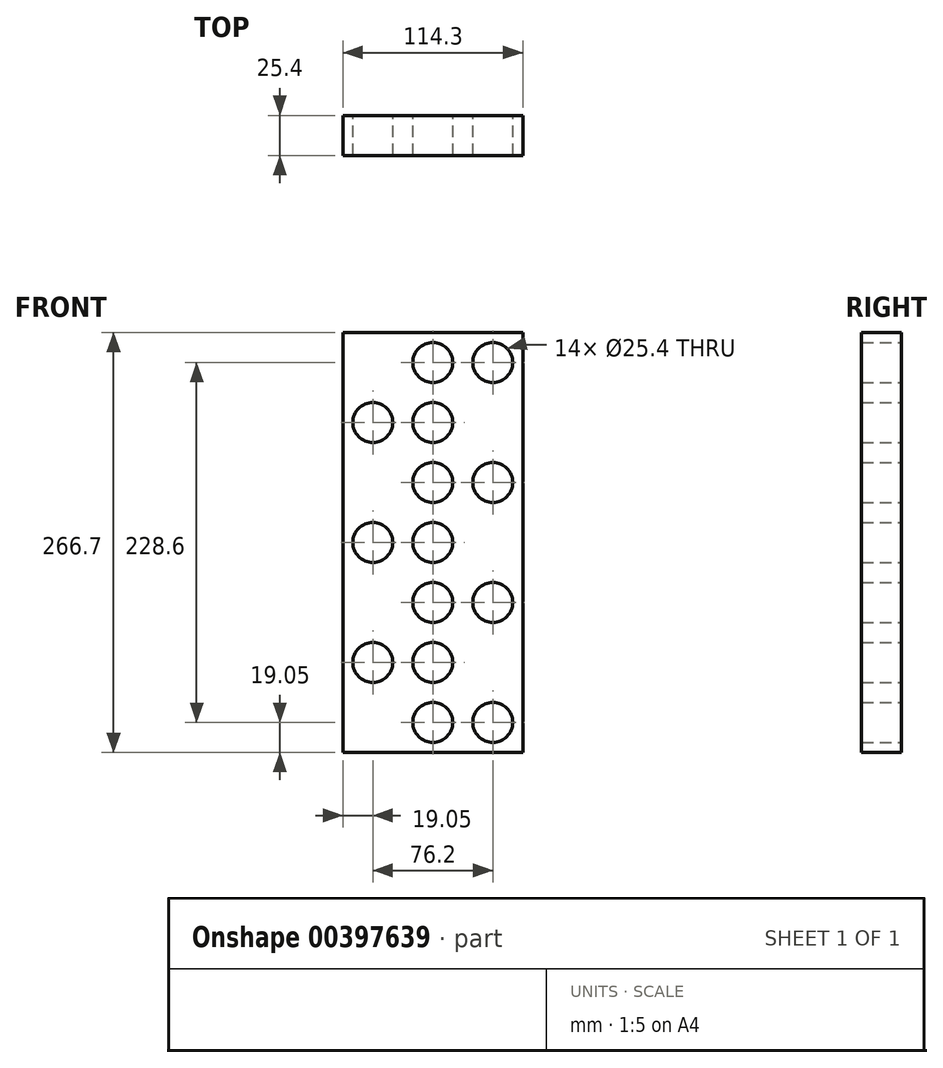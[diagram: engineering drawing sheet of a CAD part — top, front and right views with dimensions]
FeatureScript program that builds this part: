
annotation { "Feature Type Name" : "Feature", "Feature Type Description" : "" }
export const myFeature = defineFeature(function(context is Context, id is Id, definition is map)
    precondition{}
    {
        {
            var Q0;
            Q0=qCreatedBy(makeId("Front.planeOp"),FACE);
            var sketch = newSketch(context, id + "F0", { "sketchPlane" : qUnion([Q0])});
            skLineSegment(sketch, "E0.bottom", {"start": v(0, 0) * mm, "end": v(-114.3, 0) * mm});
            skLineSegment(sketch, "E0.top", {"start": v(0, 266.7) * mm, "end": v(-114.3, 266.7) * mm});
            skLineSegment(sketch, "E0.left", {"start": v(0, 0) * mm, "end": v(0, 266.7) * mm});
            skLineSegment(sketch, "E0.right", {"start": v(-114.3, 0) * mm, "end": v(-114.3, 266.7) * mm});
            skSolve(sketch);
        }
        {
            var Q0;
            Q0=qCreatedBy(makeId("Front.planeOp"),FACE);
            var sketch = newSketch(context, id + "F1", { "sketchPlane" : qUnion([Q0])});
            skLineSegment(sketch, "E1", {"start": v(0, 0) * mm, "end": v(-19.05, 0) * mm});
            skLineSegment(sketch, "E2", {"start": v(0, 0) * mm, "end": v(-57.15, 0) * mm});
            skPoint(sketch, "E2.endSnap0", {"position": v(-9.53, 0) * mm});
            skLineSegment(sketch, "E3", {"start": v(0, 0) * mm, "end": v(-95.25, 0) * mm});
            skLineSegment(sketch, "E4", {"start": v(-19.05, 0) * mm, "end": v(-19.05, 19.05) * mm});
            skLineSegment(sketch, "E5", {"start": v(-95.25, 0) * mm, "end": v(-95.25, 19.05) * mm});
            skLineSegment(sketch, "E6", {"start": v(-57.15, 0) * mm, "end": v(-57.15, 19.05) * mm});
            skCircle(sketch, "E7", {"center": v(-19.05, 19.05) * mm, "radius": 12.7 * mm});
            skCircle(sketch, "E8", {"center": v(-57.15, 19.05) * mm, "radius": 12.7 * mm});
            skCircle(sketch, "E9.0.1.0", {"center": v(-57.15, 57.15) * mm, "radius": 12.7 * mm});
            skCircle(sketch, "E9.0.1.1", {"center": v(-95.25, 57.15) * mm, "radius": 12.7 * mm});
            skLineSegment(sketch, "E9.direction1", {"start": v(-95.25, 19.05) * mm, "end": v(-69.85, 19.05) * mm, "construction": true});
            skLineSegment(sketch, "E9.direction2", {"start": v(-95.25, 19.05) * mm, "end": v(-95.25, 57.15) * mm, "construction": true});
            skCircle(sketch, "E10.0.1.0", {"center": v(-19.05, 95.25) * mm, "radius": 12.7 * mm});
            skCircle(sketch, "E10.0.1.1", {"center": v(-57.15, 95.25) * mm, "radius": 12.7 * mm});
            skLineSegment(sketch, "E10.direction1", {"start": v(-57.15, 19.05) * mm, "end": v(-31.75, 19.05) * mm, "construction": true});
            skLineSegment(sketch, "E10.direction2", {"start": v(-57.15, 19.05) * mm, "end": v(-57.15, 95.25) * mm, "construction": true});
            skCircle(sketch, "E11.0.1.0", {"center": v(-95.25, 133.35) * mm, "radius": 12.7 * mm});
            skCircle(sketch, "E11.0.1.1", {"center": v(-57.15, 133.35) * mm, "radius": 12.7 * mm});
            skCircle(sketch, "E11.0.2.0", {"center": v(-95.25, 209.55) * mm, "radius": 12.7 * mm});
            skCircle(sketch, "E11.0.2.1", {"center": v(-57.15, 209.55) * mm, "radius": 12.7 * mm});
            skLineSegment(sketch, "E11.direction1", {"start": v(-95.25, 57.15) * mm, "end": v(-69.85, 57.15) * mm, "construction": true});
            skLineSegment(sketch, "E11.direction2", {"start": v(-95.25, 57.15) * mm, "end": v(-95.25, 133.35) * mm, "construction": true});
            skCircle(sketch, "E12.0.0.2", {"center": v(-19.05, 171.45) * mm, "radius": 12.7 * mm});
            skCircle(sketch, "E12.2.0.2", {"center": v(-57.15, 171.45) * mm, "radius": 12.7 * mm});
            skCircle(sketch, "E13.0.0.3", {"center": v(-19.05, 247.65) * mm, "radius": 12.7 * mm});
            skCircle(sketch, "E13.2.0.3", {"center": v(-57.15, 247.65) * mm, "radius": 12.7 * mm});
            skLineSegment(sketch, "E14.direction1", {"start": v(-95.25, 209.55) * mm, "end": v(-69.85, 209.55) * mm, "construction": true});
            skLineSegment(sketch, "E14.direction2", {"start": v(-95.25, 209.55) * mm, "end": v(-95.25, 247.65) * mm, "construction": true});
            skSolve(sketch);
        }
        {
            var Q0;
            Q0 = qSketchRegion(id + "F0", true);
            extrude(context, id + "F2", {"entities" : qUnion([Q0]), "depth" : 25.4 * mm});
        }
        {
            var Q0;
            Q0 = qSketchRegion(id + "F1", true);
            extrude(context, id + "F3", {"entities" : qUnion([Q0]), "operationType" : NewBodyOperationType.REMOVE, "depth" : 25.4 * mm});
        }
    });
